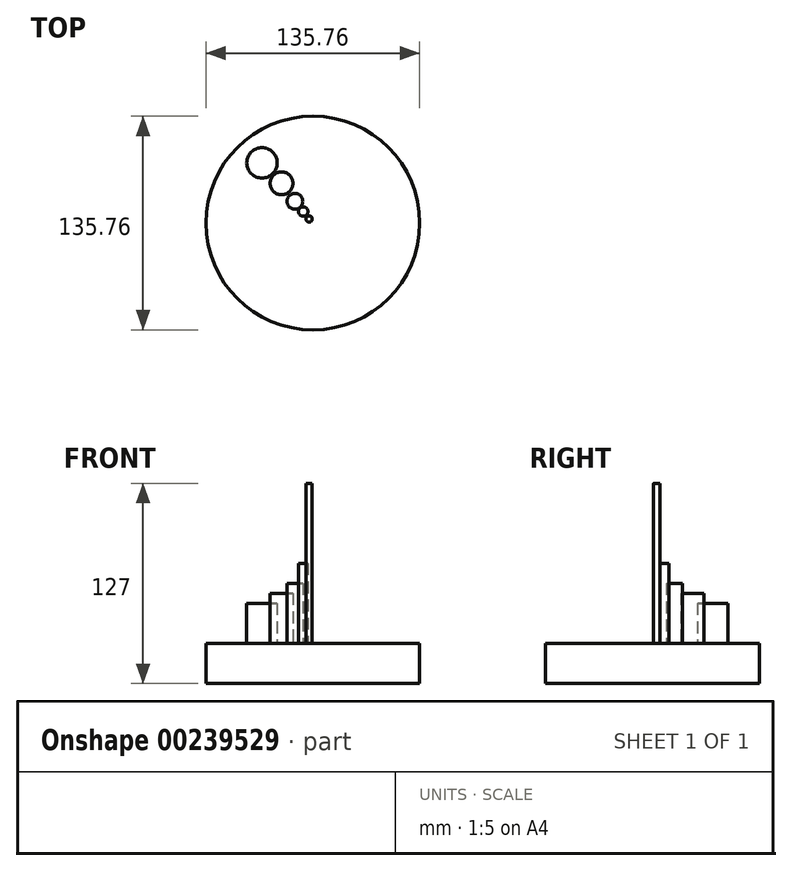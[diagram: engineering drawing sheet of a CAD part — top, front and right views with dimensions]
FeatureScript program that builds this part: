
annotation { "Feature Type Name" : "Feature", "Feature Type Description" : "" }
export const myFeature = defineFeature(function(context is Context, id is Id, definition is map)
    precondition{}
    {
        {
            var Q0;
            Q0=qCreatedBy(makeId("Top.planeOp"),FACE);
            var sketch = newSketch(context, id + "F0", { "sketchPlane" : qUnion([Q0])});
            skCircle(sketch, "E0", {"center": v(0, 0) * mm, "radius": 67.88 * mm});
            skSolve(sketch);
        }
        {
            var Q0;
            Q0 = qSketchRegion(id + "F0", true);
            extrude(context, id + "F1", {"entities" : qUnion([Q0]), "endBound" : BoundingType.SYMMETRIC, "depth" : 25.4 * mm});
        }
        {
            var Q0;
            Q0=makeQuery(id+"F1.opExtrude","CAP_FACE",FACE,{"disambiguationData":[OSD([sQuery(id+"F0.wireOp",EDGE,"E0")])],"isStart":false});
            var sketch = newSketch(context, id + "F2", { "sketchPlane" : qUnion([Q0])});
            skCircle(sketch, "E1", {"center": v(-32.32, 38.23) * mm, "radius": 9.66 * mm});
            skSolve(sketch);
        }
        {
            var Q0;
            Q0 = qSketchRegion(id + "F2", true);
            extrude(context, id + "F3", {"entities" : qUnion([Q0]), "operationType" : NewBodyOperationType.ADD, "depth" : 25.4 * mm});
        }
        {
            var Q0;
            Q0=makeQuery(id+"F1.opExtrude","CAP_FACE",FACE,{"disambiguationData":[OSD([sQuery(id+"F0.wireOp",EDGE,"E0")])],"isStart":false});
            var sketch = newSketch(context, id + "F4", { "sketchPlane" : qUnion([Q0])});
            skCircle(sketch, "E2", {"center": v(-19.9, 25.22) * mm, "radius": 7.27 * mm});
            skSolve(sketch);
        }
        {
            var Q0;
            Q0 = qSketchRegion(id + "F4", true);
            extrude(context, id + "F5", {"entities" : qUnion([Q0]), "operationType" : NewBodyOperationType.ADD, "depth" : 31.75 * mm});
        }
        {
            var Q0;
            Q0=makeQuery(id+"F1.opExtrude","CAP_FACE",FACE,{"disambiguationData":[OSD([sQuery(id+"F0.wireOp",EDGE,"E0")])],"isStart":false});
            var sketch = newSketch(context, id + "F6", { "sketchPlane" : qUnion([Q0])});
            skCircle(sketch, "E3", {"center": v(-11.43, 13.8) * mm, "radius": 5.02 * mm});
            skSolve(sketch);
        }
        {
            var Q0;
            Q0 = qSketchRegion(id + "F6", true);
            extrude(context, id + "F7", {"entities" : qUnion([Q0]), "operationType" : NewBodyOperationType.ADD, "depth" : 38.1 * mm});
        }
        {
            var Q0;
            Q0=makeQuery(id+"F1.opExtrude","CAP_FACE",FACE,{"disambiguationData":[OSD([sQuery(id+"F0.wireOp",EDGE,"E0")])],"isStart":false});
            var sketch = newSketch(context, id + "F8", { "sketchPlane" : qUnion([Q0])});
            skCircle(sketch, "E4", {"center": v(-6.1, 7.3) * mm, "radius": 3 * mm});
            skSolve(sketch);
        }
        {
            var Q0;
            Q0 = qSketchRegion(id + "F8", true);
            extrude(context, id + "F9", {"entities" : qUnion([Q0]), "operationType" : NewBodyOperationType.ADD, "depth" : 50.8 * mm});
        }
        {
            var Q0;
            Q0=makeQuery(id+"F1.opExtrude","CAP_FACE",FACE,{"disambiguationData":[OSD([sQuery(id+"F0.wireOp",EDGE,"E0")])],"isStart":false});
            var sketch = newSketch(context, id + "F10", { "sketchPlane" : qUnion([Q0])});
            skCircle(sketch, "E5", {"center": v(-2.36, 2.56) * mm, "radius": 1.98 * mm});
            skSolve(sketch);
        }
        {
            var Q0;
            Q0 = qSketchRegion(id + "F10", true);
            extrude(context, id + "F11", {"entities" : qUnion([Q0]), "operationType" : NewBodyOperationType.ADD, "depth" : 101.6 * mm});
        }
    });
